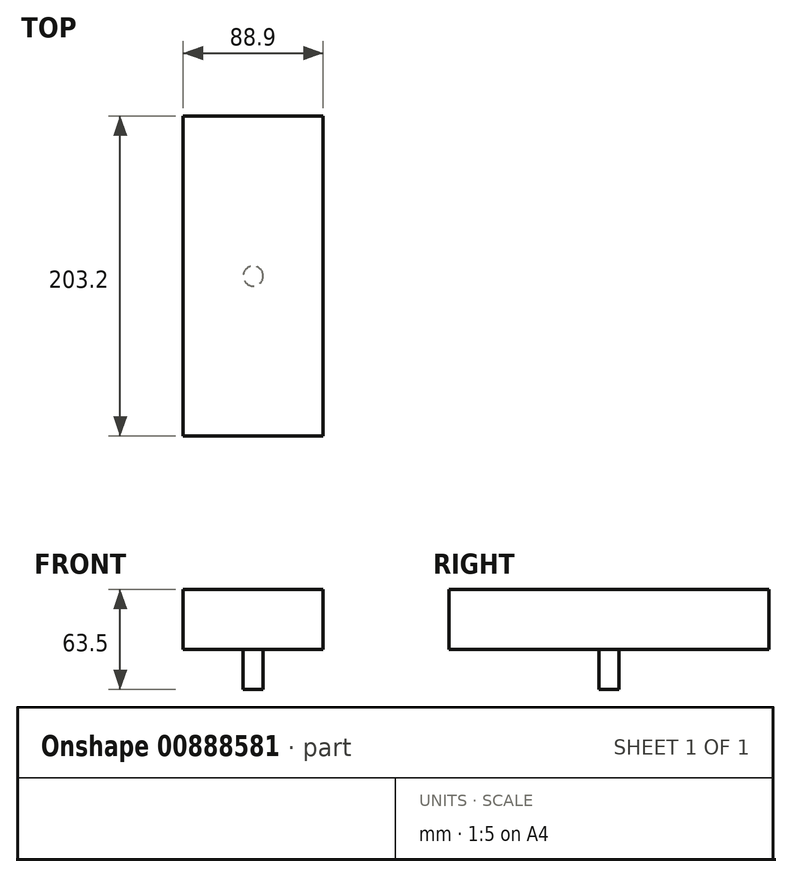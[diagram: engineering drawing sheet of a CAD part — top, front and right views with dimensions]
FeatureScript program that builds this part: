
annotation { "Feature Type Name" : "Feature", "Feature Type Description" : "" }
export const myFeature = defineFeature(function(context is Context, id is Id, definition is map)
    precondition{}
    {
        {
            var Q0;
            Q0=qCreatedBy(makeId("Top.planeOp"),FACE);
            var sketch = newSketch(context, id + "F0", { "sketchPlane" : qUnion([Q0])});
            skLineSegment(sketch, "E0.bottom", {"start": v(44.45, -101.6) * mm, "end": v(-44.45, -101.6) * mm});
            skLineSegment(sketch, "E0.top", {"start": v(44.45, 101.6) * mm, "end": v(-44.45, 101.6) * mm});
            skLineSegment(sketch, "E0.left", {"start": v(44.45, -101.6) * mm, "end": v(44.45, 101.6) * mm});
            skLineSegment(sketch, "E0.right", {"start": v(-44.45, -101.6) * mm, "end": v(-44.45, 101.6) * mm});
            skPoint(sketch, "E0.middle", {"position": v(0, 0) * mm});
            skSolve(sketch);
        }
        {
            var Q0;
            Q0 = qSketchRegion(id + "F0", true);
            extrude(context, id + "F1", {"entities" : qUnion([Q0]), "depth" : 38.1 * mm, "offsetDistance" : 25.4 * mm});
        }
        {
            var Q0;
            Q0=qCreatedBy(makeId("Top.planeOp"),FACE);
            var sketch = newSketch(context, id + "F2", { "sketchPlane" : qUnion([Q0])});
            skCircle(sketch, "E1", {"center": v(0, 0) * mm, "radius": 6.35 * mm});
            skSolve(sketch);
        }
        {
            var Q0;
            Q0 = qSketchRegion(id + "F2", true);
            extrude(context, id + "F3", {"entities" : qUnion([Q0]), "operationType" : NewBodyOperationType.ADD, "oppositeDirection" : true, "depth" : 25.4 * mm, "offsetDistance" : 25.4 * mm});
        }
    });
